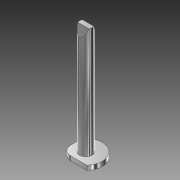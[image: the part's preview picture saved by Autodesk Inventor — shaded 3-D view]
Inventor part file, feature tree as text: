
AUTODESK INVENTOR PART (.ipt)
format: ipt  version: 2012 (Build 160160000, 160)  size: 97,792 bytes
history: native  units: mm
features: extrude x4, sketch x3
ambient origin geometry x8: Origin, YZ Plane, XZ Plane, XY Plane, X Axis, Y Axis, Z Axis, Center Point
bodies: Solid1 (feature_tree)
feature tree (7):
  extrude  "Extrusion1"  Depth=24.016mm TaperAngle=0.0deg
  sketch  "Sketch2"  dims[d3=7.1374mm d4=1.0mm d5=0.0mm]
  extrude  "Extrusion2"  Depth=1.0mm TaperAngle=0.0deg
  extrude  "Extrusion3"  Depth=2.9mm
  extrude  "Extrusion4"  TaperAngle=0.0deg  [1 undecoded]
  sketch  "Sketch1"  dims[d0=2.68mm d1=24.016mm d2=0.0mm]
  sketch  "Sketch3"  dims[d6=2.4mm d7=2.9mm d8=0.0mm d9=0.0mm d10=24.0mm d11=0.5mm d12=1.4mm d13=2.0mm d14=10.0mm d15=0.0mm d16=2.0mm]
note: 1 required parameter value undecoded (feature->parameter linkage not recoverable at this tier; creation-order binding heuristic only, values carry confidence <= 0.55)
